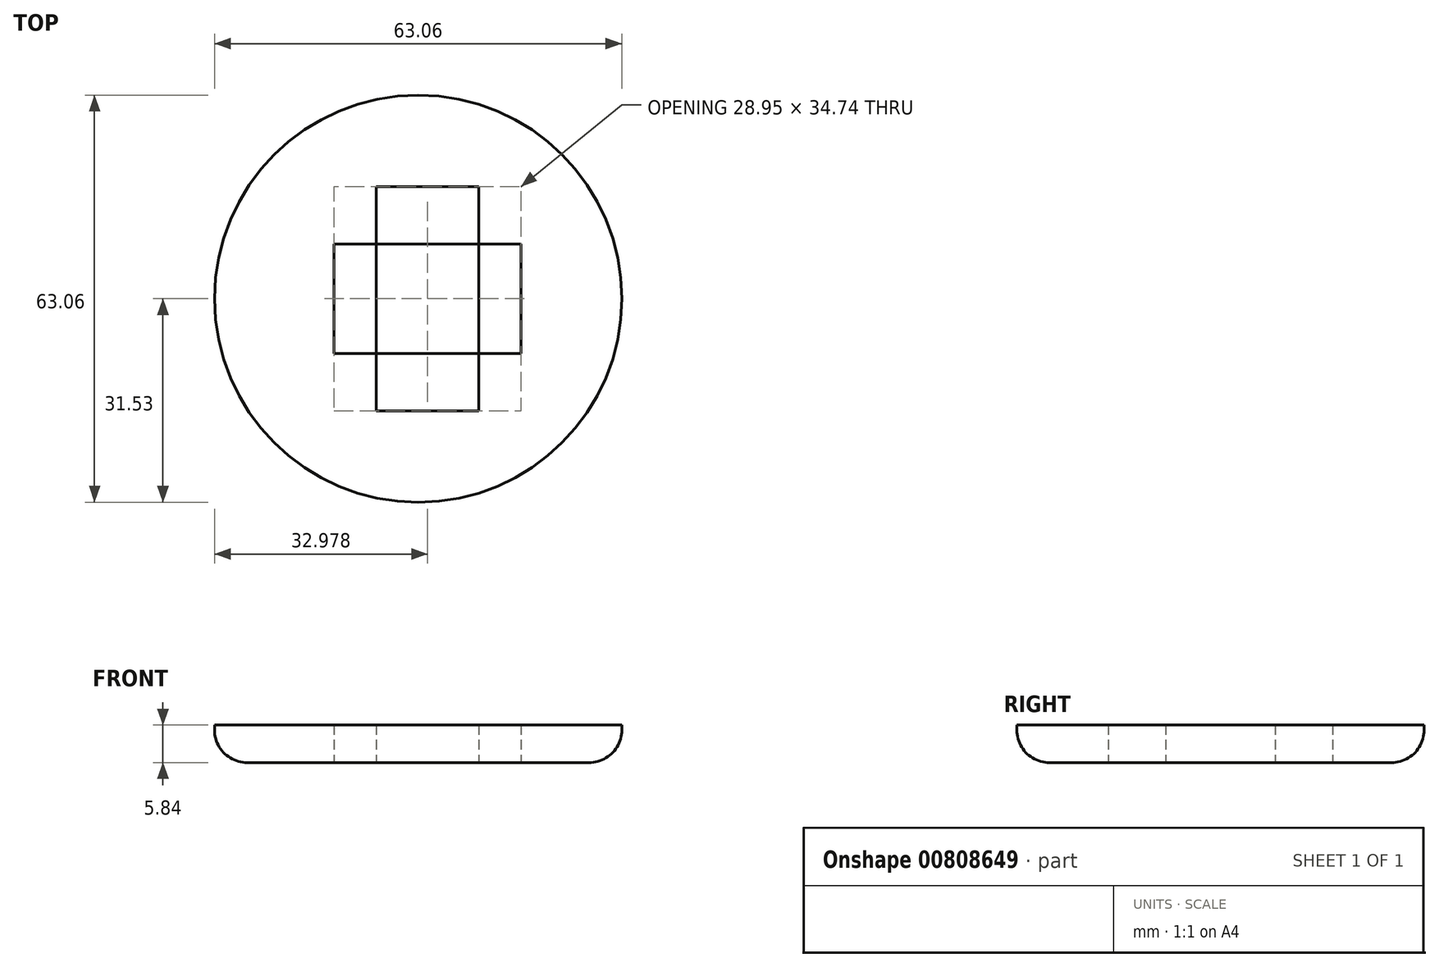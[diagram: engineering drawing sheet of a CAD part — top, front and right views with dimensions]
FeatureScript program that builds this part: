
annotation { "Feature Type Name" : "Feature", "Feature Type Description" : "" }
export const myFeature = defineFeature(function(context is Context, id is Id, definition is map)
    precondition{}
    {
        {
            var Q0;
            Q0=qCreatedBy(makeId("Top.planeOp"),FACE);
            var sketch = newSketch(context, id + "F0", { "sketchPlane" : qUnion([Q0])});
            skCircle(sketch, "E0", {"center": v(0, 0) * mm, "radius": 31.53 * mm});
            skLineSegment(sketch, "E1.bottom", {"start": v(15.92, 8.5) * mm, "end": v(-13.03, 8.5) * mm});
            skLineSegment(sketch, "E1.top", {"start": v(15.92, -8.5) * mm, "end": v(-13.03, -8.5) * mm});
            skLineSegment(sketch, "E1.left", {"start": v(15.92, 8.5) * mm, "end": v(15.92, -8.5) * mm});
            skLineSegment(sketch, "E1.right", {"start": v(-13.03, 8.5) * mm, "end": v(-13.03, -8.5) * mm});
            skPoint(sketch, "E1.middle", {"position": v(1.45, 0) * mm});
            skLineSegment(sketch, "E2.bottom", {"start": v(9.36, 17.37) * mm, "end": v(-6.47, 17.37) * mm});
            skLineSegment(sketch, "E2.top", {"start": v(9.36, -17.37) * mm, "end": v(-6.47, -17.37) * mm});
            skLineSegment(sketch, "E2.left", {"start": v(9.36, 17.37) * mm, "end": v(9.36, -17.37) * mm});
            skLineSegment(sketch, "E2.right", {"start": v(-6.47, 17.37) * mm, "end": v(-6.47, -17.37) * mm});
            skSolve(sketch);
        }
        {
            var Q0;
            {var subQ0=sQuery(id+"F0.wireOp",EDGE,"E2.left");var subQ1=sQuery(id+"F0.wireOp",EDGE,"E1.bottom");var subQ2=makeQuery(id+"F0.imprint","INTERSECT",VERTEX,{"derivedFrom":[subQ1,subQ0]});Q0=makeQuery(id+"F0.imprint","IMPRINT",FACE,{"disambiguationData":[TD([[makeQuery(id+"F0.imprint","IMPRINT",EDGE,{"disambiguationData":[TD([[subQ2,-1.0]])],"derivedFrom":subQ1}),1.0]])]});}
            var Q1;
            Q1=makeQuery(id+"F0.imprint","IMPRINT",FACE,{"disambiguationData":[TD([[makeQuery(id+"F0.imprint","IMPRINT",EDGE,{"derivedFrom":sQuery(id+"F0.wireOp",EDGE,"E0")}),1.0]])]});
            extrude(context, id + "F1", {"entities" : qUnion([Q0, Q1]), "depth" : 5.84 * mm, "offsetDistance" : 25.4 * mm});
        }
        {
            var Q0;
            Q0=makeQuery(id+"F1.opExtrude","CAP_EDGE",EDGE,{"disambiguationData":[OSD([sQuery(id+"F0.wireOp",EDGE,"E0")])],"isStart":true});
            var Q1;
            {var subQ0=sQuery(id+"F0.wireOp",EDGE,"E2.right");Q1=makeQuery(id+"F1.opExtrude","CAP_EDGE",EDGE,{"disambiguationData":[OSD([subQ0]),TDD([makeQuery(id+"F0.imprint","IMPRINT",EDGE,{"disambiguationData":[TD([[makeQuery(id+"F0.imprint","INTERSECT",VERTEX,{"derivedFrom":[sQuery(id+"F0.wireOp",EDGE,"E1.bottom"),subQ0]}),-1.0]])],"derivedFrom":subQ0})])],"isStart":true});}
            var Q2;
            Q2=makeQuery(id+"F1.opExtrude","CAP_FACE",FACE,{"disambiguationData":[OSD([sQuery(id+"F0.wireOp",EDGE,"E1.bottom"),sQuery(id+"F0.wireOp",EDGE,"E1.top"),sQuery(id+"F0.wireOp",EDGE,"E2.left"),sQuery(id+"F0.wireOp",EDGE,"E2.right")])],"isStart":false});
            var Q3;
            {var subQ0=sQuery(id+"F0.wireOp",EDGE,"E2.right");Q3=makeQuery(id+"F1.opExtrude","CAP_EDGE",EDGE,{"disambiguationData":[OSD([subQ0]),TDD([makeQuery(id+"F0.imprint","IMPRINT",EDGE,{"disambiguationData":[TD([[makeQuery(id+"F0.imprint","INTERSECT",VERTEX,{"derivedFrom":[sQuery(id+"F0.wireOp",EDGE,"E1.bottom"),subQ0]}),-1.0]])],"derivedFrom":subQ0})])],"isStart":false});}
            var Q4;
            {var subQ0=sQuery(id+"F0.wireOp",EDGE,"E1.bottom");Q4=makeQuery(id+"F1.opExtrude","CAP_EDGE",EDGE,{"disambiguationData":[OSD([subQ0]),TDD([makeQuery(id+"F0.imprint","IMPRINT",EDGE,{"disambiguationData":[TD([[makeQuery(id+"F0.imprint","INTERSECT",VERTEX,{"derivedFrom":[subQ0,sQuery(id+"F0.wireOp",EDGE,"E2.left")]}),-1.0]])],"derivedFrom":subQ0})])],"isStart":false});}
            var Q5;
            {var subQ0=sQuery(id+"F0.wireOp",EDGE,"E1.top");Q5=makeQuery(id+"F1.opExtrude","CAP_EDGE",EDGE,{"disambiguationData":[OSD([subQ0]),TDD([makeQuery(id+"F0.imprint","IMPRINT",EDGE,{"disambiguationData":[TD([[makeQuery(id+"F0.imprint","INTERSECT",VERTEX,{"derivedFrom":[subQ0,sQuery(id+"F0.wireOp",EDGE,"E2.left")]}),-1.0]])],"derivedFrom":subQ0})])],"isStart":false});}
            fillet(context, id + "F2", {"entities" : qUnion([Q0, Q1, Q2, Q3, Q4, Q5]), "radius" : 5.08 * mm, "tangentPropagation" : true, "allowEdgeOverflow" : false});
        }
    });
